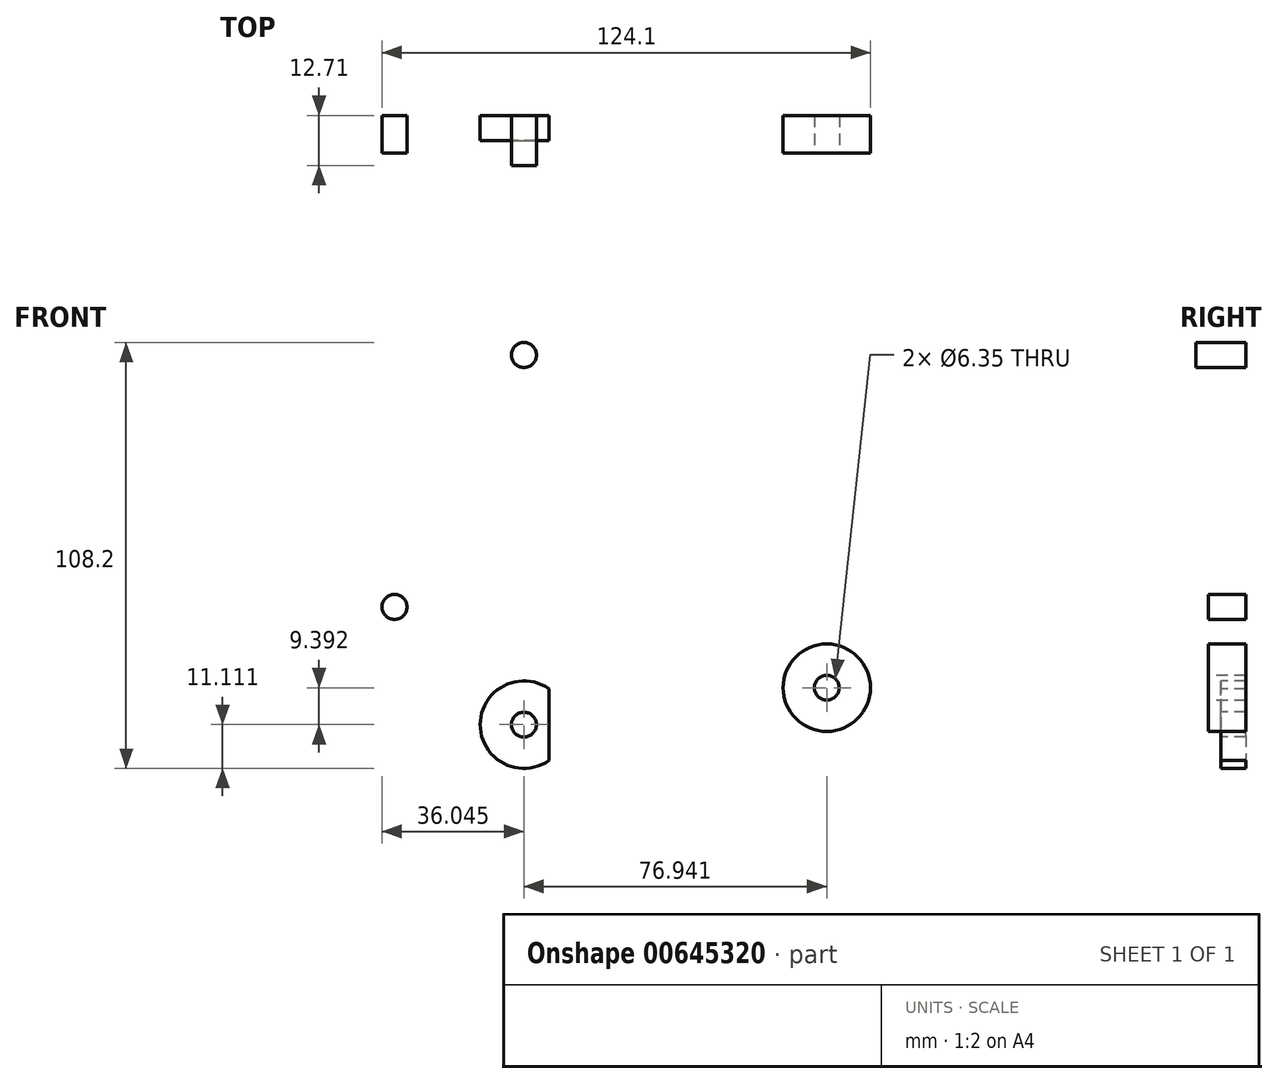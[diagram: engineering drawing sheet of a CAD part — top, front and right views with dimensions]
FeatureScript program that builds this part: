
annotation { "Feature Type Name" : "Feature", "Feature Type Description" : "" }
export const myFeature = defineFeature(function(context is Context, id is Id, definition is map)
    precondition{}
    {
        {
            var Q0;
            Q0=qCreatedBy(makeId("Front.planeOp"),FACE);
            var sketch = newSketch(context, id + "F0", { "sketchPlane" : qUnion([Q0])});
            skCircle(sketch, "E0", {"center": v(0, 0) * mm, "radius": 15.88 * mm});
            skCircle(sketch, "E1", {"center": v(34.2, -37.57) * mm, "radius": 11.11 * mm});
            skCircle(sketch, "E2", {"center": v(-42.74, 46.96) * mm, "radius": 11.11 * mm});
            skCircle(sketch, "E3", {"center": v(-75.62, 17.04) * mm, "radius": 7.94 * mm});
            skLineSegment(sketch, "E4", {"start": v(-42.74, 46.96) * mm, "end": v(-75.62, 17.04) * mm, "construction": true});
            skLineSegment(sketch, "E5", {"start": v(0, 0) * mm, "end": v(-42.74, -46.96) * mm, "construction": true});
            skCircle(sketch, "E6", {"center": v(-42.74, -46.96) * mm, "radius": 11.11 * mm});
            skLineSegment(sketch, "E7", {"start": v(-42.74, -46.96) * mm, "end": v(-75.62, -17.04) * mm, "construction": true});
            skCircle(sketch, "E8", {"center": v(-75.62, -17.04) * mm, "radius": 7.94 * mm});
            skLineSegment(sketch, "E9", {"start": v(-81.36, -22.51) * mm, "end": v(-50.8, -54.62) * mm});
            skLineSegment(sketch, "E10", {"start": v(-35.11, -55.03) * mm, "end": v(10.9, -11.54) * mm});
            skCircle(sketch, "E11", {"center": v(-28.84, -31.69) * mm, "radius": 3.18 * mm});
            skCircle(sketch, "E12", {"center": v(-42.74, 46.96) * mm, "radius": 3.18 * mm});
            skCircle(sketch, "E13", {"center": v(-42.74, -46.96) * mm, "radius": 3.18 * mm});
            skCircle(sketch, "E14", {"center": v(34.2, -37.57) * mm, "radius": 3.18 * mm});
            skCircle(sketch, "E15", {"center": v(26.93, -24.87) * mm, "radius": 3.18 * mm});
            skLineSegment(sketch, "E16", {"start": v(26.93, -24.87) * mm, "end": v(24.59, -27.01) * mm, "construction": true});
            skLineSegment(sketch, "E17", {"start": v(-35.11, 55.03) * mm, "end": v(10.9, 11.54) * mm});
            skLineSegment(sketch, "E18", {"start": v(12.69, 9.54) * mm, "end": v(43.08, -30.9) * mm});
            skCircle(sketch, "E19", {"center": v(0, 0) * mm, "radius": 3.18 * mm});
            skCircle(sketch, "E20", {"center": v(0, 0) * mm, "radius": 3.98 * mm});
            skLineSegment(sketch, "E21", {"start": v(26.72, -45.78) * mm, "end": v(-10.69, -11.74) * mm});
            skLineSegment(sketch, "E22", {"start": v(-70.7, 10.8) * mm, "end": v(-50.9, 26.4) * mm});
            skLineSegment(sketch, "E23", {"start": v(-39.72, 25.04) * mm, "end": v(-12.5, -9.78) * mm});
            skArc(sketch, "E24.filletArc", {"start": v(-39.72, 25.04) * mm, "mid": v(-45.03, 28.04) * mm, "end": v(-50.9, 26.4) * mm});
            skLineSegment(sketch, "E25", {"start": v(-70.7, -10.8) * mm, "end": v(-50.85, -26.44) * mm});
            skLineSegment(sketch, "E26", {"start": v(-10.64, 11.78) * mm, "end": v(-39.68, -25.1) * mm});
            skArc(sketch, "E27.filletArc", {"start": v(-50.85, -26.44) * mm, "mid": v(-45, -28.08) * mm, "end": v(-39.68, -25.1) * mm});
            skLineSegment(sketch, "E28", {"start": v(-81.36, 22.51) * mm, "end": v(-50.8, 54.62) * mm});
            skLineSegment(sketch, "E29", {"start": v(34.2, -37.57) * mm, "end": v(-42.74, 46.96) * mm, "construction": true});
            skLineSegment(sketch, "E30", {"start": v(-75.62, 17.04) * mm, "end": v(-75.62, -17.04) * mm, "construction": true});
            skCircle(sketch, "E31", {"center": v(-75.62, 17.04) * mm, "radius": 3.18 * mm});
            skCircle(sketch, "E32", {"center": v(-75.62, -17.04) * mm, "radius": 3.18 * mm});
            skSolve(sketch);
        }
        {
            var Q0;
            {var subQ0=sQuery(id+"F0.wireOp",EDGE,"E17");Q0=makeQuery(id+"F0.imprint","IMPRINT",FACE,{"disambiguationData":[TD([[makeQuery(id+"F0.imprint","IMPRINT",EDGE,{"derivedFrom":subQ0}),-1.0]])]});}
            var Q1;
            Q1=makeQuery(id+"F0.imprint","IMPRINT",FACE,{"disambiguationData":[TD([[makeQuery(id+"F0.imprint","IMPRINT",EDGE,{"derivedFrom":sQuery(id+"F0.wireOp",EDGE,"E15")}),-1.0]])]});
            var Q2;
            Q2=makeQuery(id+"F0.imprint","IMPRINT",FACE,{"disambiguationData":[TD([[makeQuery(id+"F0.imprint","IMPRINT",EDGE,{"derivedFrom":sQuery(id+"F0.wireOp",EDGE,"E14")}),-1.0]])]});
            var Q3;
            Q3=makeQuery(id+"F0.imprint","IMPRINT",FACE,{"disambiguationData":[TD([[makeQuery(id+"F0.imprint","IMPRINT",EDGE,{"derivedFrom":sQuery(id+"F0.wireOp",EDGE,"E20")}),-1.0]])]});
            var Q4;
            {var subQ0=sQuery(id+"F0.wireOp",EDGE,"E10");var subQ1=sQuery(id+"F0.wireOp",EDGE,"E0");var subQ2=makeQuery(id+"F0.imprint","INTERSECT",VERTEX,{"derivedFrom":[subQ1,subQ0]});Q4=makeQuery(id+"F0.imprint","IMPRINT",FACE,{"disambiguationData":[TD([[makeQuery(id+"F0.imprint","IMPRINT",EDGE,{"disambiguationData":[TD([[subQ2,1.0]])],"derivedFrom":subQ1}),-1.0]])]});}
            var Q5;
            {var subQ0=sQuery(id+"F0.wireOp",EDGE,"E23");var subQ1=sQuery(id+"F0.wireOp",EDGE,"E0");var subQ2=makeQuery(id+"F0.imprint","INTERSECT",VERTEX,{"derivedFrom":[subQ1,subQ0]});Q5=makeQuery(id+"F0.imprint","IMPRINT",FACE,{"disambiguationData":[TD([[makeQuery(id+"F0.imprint","IMPRINT",EDGE,{"disambiguationData":[TD([[subQ2,1.0]])],"derivedFrom":subQ1}),-1.0]])]});}
            var Q6;
            Q6=makeQuery(id+"F0.imprint","IMPRINT",FACE,{"disambiguationData":[TD([[makeQuery(id+"F0.imprint","IMPRINT",EDGE,{"derivedFrom":sQuery(id+"F0.wireOp",EDGE,"E12")}),-1.0]])]});
            var Q7;
            Q7=makeQuery(id+"F0.imprint","IMPRINT",FACE,{"disambiguationData":[TD([[makeQuery(id+"F0.imprint","IMPRINT",EDGE,{"derivedFrom":sQuery(id+"F0.wireOp",EDGE,"E31")}),-1.0]])]});
            var Q8;
            Q8=makeQuery(id+"F0.imprint","IMPRINT",FACE,{"disambiguationData":[TD([[makeQuery(id+"F0.imprint","IMPRINT",EDGE,{"derivedFrom":sQuery(id+"F0.wireOp",EDGE,"E19")}),-1.0]])]});
            var Q9;
            Q9 = qSketchRegion(id + "F3", true);
            extrude(context, id + "F1", {"entities" : qUnion([Q0, Q1, Q2, Q3, Q4, Q5, Q6, Q7, Q8, Q9]), "depth" : 3.17 * mm, "offsetDistance" : 25.4 * mm});
        }
        {
            var Q0;
            Q0=makeQuery(id+"F0.imprint","IMPRINT",FACE,{"disambiguationData":[TD([[makeQuery(id+"F0.imprint","IMPRINT",EDGE,{"derivedFrom":sQuery(id+"F0.wireOp",EDGE,"E20")}),-1.0]])]});
            var Q1;
            {var subQ12=sQuery(id+"F0.wireOp",EDGE,"E9");Q1=makeQuery(id+"F0.imprint","IMPRINT",FACE,{"disambiguationData":[TD([[makeQuery(id+"F0.imprint","IMPRINT",EDGE,{"derivedFrom":subQ12}),1.0]])]});}
            var Q2;
            {var subQ0=sQuery(id+"F0.wireOp",EDGE,"E23");var subQ1=sQuery(id+"F0.wireOp",EDGE,"E0");var subQ2=makeQuery(id+"F0.imprint","INTERSECT",VERTEX,{"derivedFrom":[subQ1,subQ0]});Q2=makeQuery(id+"F0.imprint","IMPRINT",FACE,{"disambiguationData":[TD([[makeQuery(id+"F0.imprint","IMPRINT",EDGE,{"disambiguationData":[TD([[subQ2,1.0]])],"derivedFrom":subQ1}),-1.0]])]});}
            var Q3;
            {var subQ0=sQuery(id+"F0.wireOp",EDGE,"E10");var subQ1=sQuery(id+"F0.wireOp",EDGE,"E0");var subQ2=makeQuery(id+"F0.imprint","INTERSECT",VERTEX,{"derivedFrom":[subQ1,subQ0]});Q3=makeQuery(id+"F0.imprint","IMPRINT",FACE,{"disambiguationData":[TD([[makeQuery(id+"F0.imprint","IMPRINT",EDGE,{"disambiguationData":[TD([[subQ2,1.0]])],"derivedFrom":subQ1}),-1.0]])]});}
            var Q4;
            Q4=makeQuery(id+"F0.imprint","IMPRINT",FACE,{"disambiguationData":[TD([[makeQuery(id+"F0.imprint","IMPRINT",EDGE,{"derivedFrom":sQuery(id+"F0.wireOp",EDGE,"E32")}),-1.0]])]});
            var Q5;
            Q5=makeQuery(id+"F0.imprint","IMPRINT",FACE,{"disambiguationData":[TD([[makeQuery(id+"F0.imprint","IMPRINT",EDGE,{"derivedFrom":sQuery(id+"F0.wireOp",EDGE,"E13")}),-1.0]])]});
            var Q6;
            Q6=makeQuery(id+"F0.imprint","IMPRINT",FACE,{"disambiguationData":[TD([[makeQuery(id+"F0.imprint","IMPRINT",EDGE,{"derivedFrom":sQuery(id+"F0.wireOp",EDGE,"E19")}),-1.0]])]});
            extrude(context, id + "F2", {"entities" : qUnion([Q0, Q1, Q2, Q3, Q4, Q5, Q6]), "oppositeDirection" : true, "depth" : 3.17 * mm, "offsetDistance" : 25.4 * mm});
        }
        {
            var Q0;
            Q0=makeQuery(id+"F1.opExtrude","CAP_FACE",FACE,{"disambiguationData":[OSD([sQuery(id+"F0.wireOp",EDGE,"E0"),sQuery(id+"F0.wireOp",EDGE,"E1"),sQuery(id+"F0.wireOp",EDGE,"E2"),sQuery(id+"F0.wireOp",EDGE,"E3"),sQuery(id+"F0.wireOp",EDGE,"E12"),sQuery(id+"F0.wireOp",EDGE,"E14"),sQuery(id+"F0.wireOp",EDGE,"E15"),sQuery(id+"F0.wireOp",EDGE,"E17"),sQuery(id+"F0.wireOp",EDGE,"E18"),sQuery(id+"F0.wireOp",EDGE,"E19"),sQuery(id+"F0.wireOp",EDGE,"E21"),sQuery(id+"F0.wireOp",EDGE,"E22"),sQuery(id+"F0.wireOp",EDGE,"E23"),sQuery(id+"F0.wireOp",EDGE,"E24.filletArc"),sQuery(id+"F0.wireOp",EDGE,"E26"),sQuery(id+"F0.wireOp",EDGE,"E28"),sQuery(id+"F0.wireOp",EDGE,"E31")])],"isStart":false});
            var sketch = newSketch(context, id + "F3", { "sketchPlane" : qUnion([Q0])});
            skCircle(sketch, "E33", {"center": v(-42.74, 46.96) * mm, "radius": 3.98 * mm});
            skCircle(sketch, "E34", {"center": v(0, 0) * mm, "radius": 3.98 * mm});
            skCircle(sketch, "E35", {"center": v(34.2, -37.57) * mm, "radius": 11.11 * mm});
            skSolve(sketch);
        }
        {
            var Q0;
            Q0=makeQuery(id+"F2.opExtrude","CAP_FACE",FACE,{"disambiguationData":[OSD([sQuery(id+"F0.wireOp",EDGE,"E0"),sQuery(id+"F0.wireOp",EDGE,"E6"),sQuery(id+"F0.wireOp",EDGE,"E8"),sQuery(id+"F0.wireOp",EDGE,"E9"),sQuery(id+"F0.wireOp",EDGE,"E10"),sQuery(id+"F0.wireOp",EDGE,"E11"),sQuery(id+"F0.wireOp",EDGE,"E13"),sQuery(id+"F0.wireOp",EDGE,"E19"),sQuery(id+"F0.wireOp",EDGE,"E25"),sQuery(id+"F0.wireOp",EDGE,"E26"),sQuery(id+"F0.wireOp",EDGE,"E27.filletArc"),sQuery(id+"F0.wireOp",EDGE,"E32")])],"isStart":true});
            var sketch = newSketch(context, id + "F4", { "sketchPlane" : qUnion([Q0])});
            skCircle(sketch, "E36", {"center": v(-42.74, -46.96) * mm, "radius": 11.11 * mm});
            skCircle(sketch, "E37", {"center": v(-75.62, -17.04) * mm, "radius": 3.98 * mm});
            skLineSegment(sketch, "E38", {"start": v(-36.4, -37.84) * mm, "end": v(-36.4, -56.08) * mm});
            skLineSegment(sketch, "E39", {"start": v(-36.4, -46.96) * mm, "end": v(34.2, -37.57) * mm, "construction": true});
            skSolve(sketch);
        }
        {
            var Q0;
            Q0=qCreatedBy(makeId("Front.planeOp"),FACE);
            cPlane(context, id + "F5", {"entities" : qUnion([Q0]), "cplaneType" : CPlaneType.OFFSET, "offset" : 9.52 * mm, "oppositeDirection" : true, "width" : 152.4 * mm, "height" : 152.4 * mm});
        }
        {
            var Q0;
            {var subQ2=sQuery(id+"F4.wireOp",EDGE,"E38");Q0=makeQuery(id+"F4.imprint","IMPRINT",FACE,{"disambiguationData":[TD([[makeQuery(id+"F4.imprint","IMPRINT",EDGE,{"derivedFrom":subQ2}),-1.0]])]});}
            var Q1;
            Q1=makeQuery(id+"F3.imprint","IMPRINT",FACE,{"disambiguationData":[TD([[makeQuery(id+"F3.imprint","IMPRINT",EDGE,{"derivedFrom":makeQuery(id+"F1.opExtrude","CAP_EDGE",EDGE,{"disambiguationData":[OSD([sQuery(id+"F0.wireOp",EDGE,"E14")])],"isStart":false})}),-1.0]])]});
            var Q2;
            Q2=makeQuery(id+"F3.imprint","IMPRINT",FACE,{"disambiguationData":[TD([[makeQuery(id+"F3.imprint","IMPRINT",EDGE,{"derivedFrom":makeQuery(id+"F1.opExtrude","CAP_EDGE",EDGE,{"disambiguationData":[OSD([sQuery(id+"F0.wireOp",EDGE,"E12")])],"isStart":false})}),1.0]])]});
            var Q3;
            Q3=makeQuery(id+"F4.imprint","IMPRINT",FACE,{"disambiguationData":[TD([[makeQuery(id+"F4.imprint","IMPRINT",EDGE,{"derivedFrom":makeQuery(id+"F2.opExtrude","CAP_EDGE",EDGE,{"disambiguationData":[OSD([sQuery(id+"F0.wireOp",EDGE,"E32")])],"isStart":true})}),1.0]])]});
            var Q4;
            Q4=qCreatedBy(id+"F5.planeOp",FACE);
            extrude(context, id + "F6", {"entities" : qUnion([Q0, Q1, Q2, Q3]), "endBound" : BoundingType.UP_TO_SURFACE, "oppositeDirection" : true, "depth" : 25.4 * mm, "endBoundEntityFace" : qUnion([Q4]), "offsetDistance" : 25.4 * mm});
        }
        {
            var Q0;
            Q0=makeQuery(id+"F1.opExtrude","SWEPT_BODY",BODY,{"disambiguationData":[OSD([sQuery(id+"F0.wireOp",EDGE,"E0"),sQuery(id+"F0.wireOp",EDGE,"E1"),sQuery(id+"F0.wireOp",EDGE,"E2"),sQuery(id+"F0.wireOp",EDGE,"E3"),sQuery(id+"F0.wireOp",EDGE,"E12"),sQuery(id+"F0.wireOp",EDGE,"E14"),sQuery(id+"F0.wireOp",EDGE,"E15"),sQuery(id+"F0.wireOp",EDGE,"E17"),sQuery(id+"F0.wireOp",EDGE,"E18"),sQuery(id+"F0.wireOp",EDGE,"E19"),sQuery(id+"F0.wireOp",EDGE,"E21"),sQuery(id+"F0.wireOp",EDGE,"E22"),sQuery(id+"F0.wireOp",EDGE,"E23"),sQuery(id+"F0.wireOp",EDGE,"E24.filletArc"),sQuery(id+"F0.wireOp",EDGE,"E26"),sQuery(id+"F0.wireOp",EDGE,"E28"),sQuery(id+"F0.wireOp",EDGE,"E31")])]});
            var Q1;
            Q1=makeQuery(id+"F2.opExtrude","SWEPT_BODY",BODY,{"disambiguationData":[OSD([sQuery(id+"F0.wireOp",EDGE,"E0"),sQuery(id+"F0.wireOp",EDGE,"E6"),sQuery(id+"F0.wireOp",EDGE,"E8"),sQuery(id+"F0.wireOp",EDGE,"E9"),sQuery(id+"F0.wireOp",EDGE,"E10"),sQuery(id+"F0.wireOp",EDGE,"E11"),sQuery(id+"F0.wireOp",EDGE,"E13"),sQuery(id+"F0.wireOp",EDGE,"E19"),sQuery(id+"F0.wireOp",EDGE,"E25"),sQuery(id+"F0.wireOp",EDGE,"E26"),sQuery(id+"F0.wireOp",EDGE,"E27.filletArc"),sQuery(id+"F0.wireOp",EDGE,"E32")])]});
            var Q2;
            Q2=makeQuery(id+"F6.opExtrude","SWEPT_BODY",BODY,{"disambiguationData":[OSD([sQuery(id+"F0.wireOp",EDGE,"E12")])]});
            var Q3;
            Q3=makeQuery(id+"F6.opExtrude","SWEPT_BODY",BODY,{"disambiguationData":[OSD([sQuery(id+"F0.wireOp",EDGE,"E32")])]});
            var Q4;
            Q4=makeQuery(id+"F6.opExtrude","SWEPT_BODY",BODY,{"disambiguationData":[OSD([sQuery(id+"F0.wireOp",EDGE,"E13"),sQuery(id+"F4.wireOp",EDGE,"E36"),sQuery(id+"F4.wireOp",EDGE,"E38")])]});
            var Q5;
            Q5=makeQuery(id+"F6.opExtrude","SWEPT_BODY",BODY,{"disambiguationData":[OSD([sQuery(id+"F0.wireOp",EDGE,"E14"),sQuery(id+"F3.wireOp",EDGE,"E35")])]});
            booleanBodies(context, id + "F7", {"operationType" : BooleanOperationType.SUBTRACTION, "tools" : qUnion([Q0, Q1]), "targets" : qUnion([Q2, Q3, Q4, Q5])});
        }
    });
